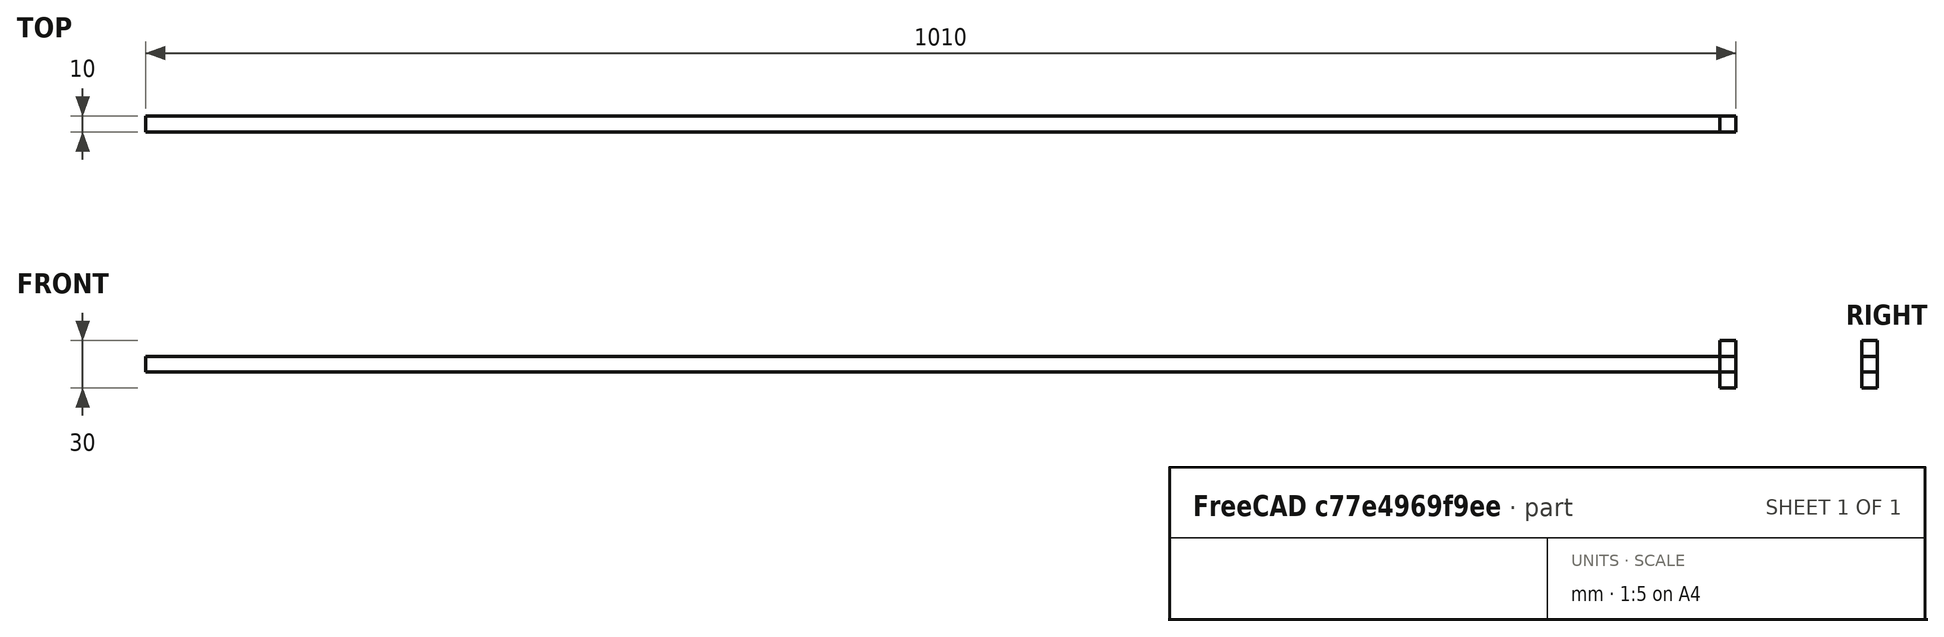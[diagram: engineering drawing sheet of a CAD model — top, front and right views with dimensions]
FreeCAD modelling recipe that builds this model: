
FCSTD DOCUMENT  (FreeCAD 0.21R33694 (Git))
Label: Buckling
License: All rights reserved
LicenseURL: http://en.wikipedia.org/wiki/All_rights_reserved
objects: Part::Box×2, Fem::FemMeshObjectPython×2, Fem::ConstraintFixed×1, Fem::FemSolverObjectPython×1, Part::FeaturePython×1, Fem::ConstraintDisplacement×1, Fem::ConstraintForce×1, Fem::FemResultObjectPython×1, App::MaterialObjectPython×1, Fem::FemAnalysis×1
note: 3 computed .brp shape members not serialized (recipe doc carries the construction recipe); baked Part::Feature solids carry a one-line shape summary decoded from their .brp

FEATURE [Part::Box] Box  label="Cube"
  AttacherType = Attacher::AttachEngine3D
  Height = 10
  Length = 1010
  Width = 10
FEATURE [Fem::ConstraintFixed] ConstraintFixed
  NormalDirection = (-1,0,0)
  Normals = (9) [(-1,0,0),(-1,0,0),(-1,0,0),(-1,0,0),(-1,0,0),(-1,0,0),(-1,0,0),(-1,0,0),(-1,0,0)]
  Points = (9) [(0,10,0),(0,10,5),(0,10,10),(0,5,0),(0,5,5),(0,5,10),(0,0,0),(0,0,5),(0,0,10)]
  References = -> [Box]
FEATURE [Fem::FemSolverObjectPython] SolverCcxTools  # FEM object (typed FeaturePython)
  AnalysisType = 0
  BeamShellResultOutput3D = false
  BucklingFactors = 1
  EigenmodeHighLimit = 1000000
  EigenmodeLowLimit = 0
  EigenmodesCount = 10
  GeometricalNonlinearity = 0
  IterationsControlParameterCutb = 0.25,0.5,0.75,0.85,,,1.5,
  IterationsControlParameterIter = 4,8,9,200,10,400,,200,,
  IterationsControlParameterTimeUse = false
  IterationsThermoMechMaximum = 2000
  IterationsUserDefinedIncrementations = false
  IterationsUserDefinedTimeStepLength = false
  MaterialNonlinearity = 0
  MatrixSolverType = 0
  SplitInputWriter = false
  ThermoMechSteadyState = true
  TimeEnd = 1
  TimeInitialStep = 0.01
FEATURE [Part::Box] Box001  label="Cube001"
  AttacherType = Attacher::AttachEngine3D
  Height = 30
  Length = 10
  Placement = pos=(1000,0,-10) rot=(0,0,1;0rad)
  Width = 10
FEATURE [Part::FeaturePython] BooleanFragments  # WARN: FeaturePython — macro-defined, semantics opaque (R4)
  Mode = 2
  Objects = -> [Box,Box001]
  Tolerance = 0
FEATURE [Fem::FemMeshObjectPython] FEMMeshGmsh  # FEM object (typed FeaturePython)
  Algorithm2D = 0
  Algorithm3D = 0
  CharacteristicLengthMax = 50
  CharacteristicLengthMin = 0
  CoherenceMesh = true
  ElementDimension = 0
  ElementOrder = 1
  GeometryTolerance = 1e-06
  GroupsOfNodes = false
  HighOrderOptimize = 0
  MeshSizeFromCurvature = 12
  OptimizeNetgen = false
  OptimizeStd = true
  Part = -> BooleanFragments
  RecombinationAlgorithm = 0
  Recombine3DAll = false
  RecombineAll = false
  SecondOrderLinear = false
FEATURE [Fem::ConstraintDisplacement] ConstraintDisplacement
  NormalDirection = (0,-1,0)
  Normals = (42) [(0,-1,0),(0,-1,0),(0,-1,0),(0,-1,0),(0,-1,0),(0,-1,0),(0,-1,0),(0,-1,0),(0,-1,0),(0,-1,0),(0,-1,0),(0,-1,0),(0,-1,0),(0,-1,0),(0,-1,0),(0,-1,0),+26 more]
  Points = (42) [(0,0,0),(0,0,5),(0,0,10),(250,0,0),(250,0,5),(250,0,10),(500,0,0),(500,0,5),(500,0,10),(750,0,0),(750,0,5),(750,0,10),(1000,0,0),(1000,0,5),+28 more]
  References = -> [BooleanFragments]
  hasXFormula = false
  hasYFormula = false
  hasZFormula = false
  rotxFix = false
  rotxFree = true
  rotyFix = false
  rotyFree = true
  rotzFix = false
  rotzFree = true
  useFlowSurfaceForce = false
  xDisplacement = 0
  xFix = false
  xFree = true
  xRotation = 0
  yDisplacement = 0
  yFix = false
  yFree = false
  yRotation = 0
  zDisplacement = 0
  zFix = false
  zFree = true
  zRotation = 0
FEATURE [Fem::ConstraintForce] ConstraintForce
  DirectionVector = (-1,0,0)
  Force = 100
  NormalDirection = (1,0,0)
  Points = (9) [(1010,10,0),(1010,10,5),(1010,10,10),(1010,5,0),(1010,5,5),(1010,5,10),(1010,0,0),(1010,0,5),(1010,0,10)]
  References = -> [BooleanFragments]
  Reversed = true
FEATURE [Fem::FemMeshObjectPython] Result_Mesh_Volume  # FEM object (typed FeaturePython)
FEATURE [Fem::FemResultObjectPython] ResultMechanical  # FEM object (typed FeaturePython)
  DisplacementLengths = [0,0,0,0,4.76212e-05,4.75213e-05,4.74994e-05,4.76022e-05,4.79048e-05,4.78183e-05,4.79231e-05,4.78266e-05,4.77731e-05,4.77864e-05,4.77736e-05,4.77773e-05,4.75155e-05,4.7511e-05,4.75391e-05,4.75242e-05,0,0,0,0,1.80041e-06,4.28452e-06,+515 more]
  DisplacementVectors = (541) [(0,0,0),(0,0,0),(0,0,0),(0,0,0),(-4.7128e-05,0,-6.83612e-06),(-4.70592e-05,0,-6.61065e-06),(-4.70374e-05,1.99811e-07,-6.6061e-06),+534 more]
  Eigenmode = 0
  EigenmodeFrequency = 0
  Mesh = -> Result_Mesh_Volume
  NodeNumbers = [1,2,3,4,5,6,7,8,9,10,11,12,13,14,15,16,17,18,19,20,21,22,23,24,25,26,27,28,29,30,31,32,33,34,35,36,37,38,39,40,41,42,43,44,45,46,47,48,49,50,51,52,53,54,55,56,57,58,59,60,61,62,63,64,65,66,67,68,69,+472 more]
  NodeStressXX = [-0.0115189,-0.0111231,-0.011315,-0.0124964,-0.00711216,-0.00674281,-0.00674759,-0.00697981,-0.00512173,-0.00509802,-0.00527141,-0.00525368,0.000266108,0.000327351,0.000222415,0.000343013,0.000270281,0.000328966,0.000227261,0.000339741,+521 more]
  NodeStressXY = [1.93772e-05,5.2995e-05,0.000491404,0.000576533,-0.000179483,-0.000150774,-0.000385579,-0.0003567,2.11194e-05,3.20718e-05,0.000130806,0.00011861,2.86245e-05,9.0938e-05,-1.77855e-05,-5.21294e-05,9.12932e-06,8.76715e-05,-1.16739e-05,+522 more]
  NodeStressXZ = [0.000255073,-0.000120745,0.000139166,-0.000269631,0.000589448,-0.000651232,-0.00038121,0.000332789,-0.0010612,0.00106572,-0.00118668,0.00119081,-0.000294732,-0.000236412,0.0002402,0.000290883,0.00027941,0.000241293,-0.000238933,+522 more]
  NodeStressYY = [-0.00780583,-0.00696491,-0.00760245,-0.00943376,0.000425171,0.00054279,0.000790274,0.000767235,-0.000169382,-0.00018374,-4.86178e-05,-3.97052e-05,0.000132556,-9.59353e-05,-0.000117878,-0.000131847,0.000109728,-9.62957e-05,-0.000125661,+522 more]
  NodeStressYZ = [6.67428e-05,-0.000137824,-0.000111285,-5.97319e-05,0.000140443,-0.00014828,-0.000585401,0.000526377,0.000281349,-0.000287904,0.000634566,-0.000626278,8.22137e-05,-0.000186874,-3.03949e-06,-0.000183977,-5.41927e-05,0.000183969,1.86707e-05,+522 more]
  NodeStressZZ = [-0.00789868,-0.00700667,-0.00739318,-0.00942561,0.000290382,0.000510985,0.00129603,0.00116201,-0.00114967,-0.0011609,-7.92996e-05,-9.05062e-05,0.000212518,4.95388e-05,0.00024324,0.000106907,0.000225218,5.73257e-05,0.000257605,0.000103076,+521 more]
  ResultType = Fem::ResultMechanical
  Stats = [-4.75506e-05,0,-3.25268e-08,2.77146e-07,-6.9399e-06,8.35915e-08,0,4.80346e-05,0,0,0,0,0,0,0,0,0,0,0,0,0,0,0,0,0,0]
  Time = 0
FEATURE [App::MaterialObjectPython] MaterialSolid  # material (typed FeaturePython)
  Category = 0
  Material = AuthorAndLicense=(c) 2014 M. Münch - GNU Lesser General Public License (LGPL),CardName=Steel-St-E-315,Density=7800 kg/m^3,Father=Metal,+13 more (map truncated)
FEATURE [Fem::FemAnalysis] Analysis
  Group = -> [ConstraintFixed,SolverCcxTools,FEMMeshGmsh,ConstraintDisplacement,ConstraintForce,ResultMechanical,MaterialSolid]
